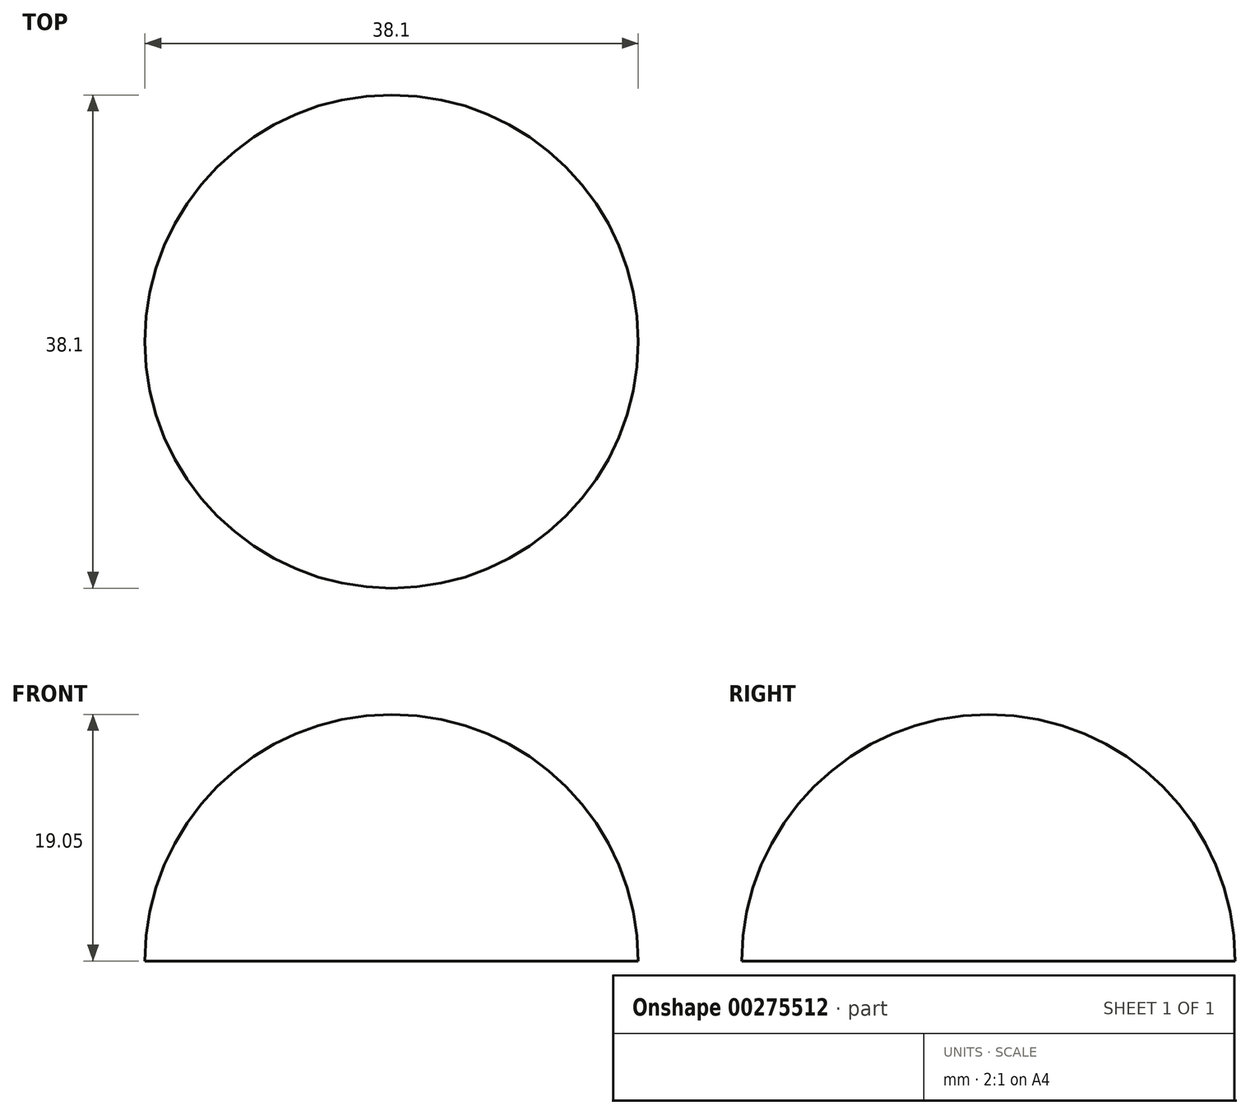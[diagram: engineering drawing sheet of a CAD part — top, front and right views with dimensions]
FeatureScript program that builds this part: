
annotation { "Feature Type Name" : "Feature", "Feature Type Description" : "" }
export const myFeature = defineFeature(function(context is Context, id is Id, definition is map)
    precondition{}
    {
        {
            var Q0;
            Q0=qCreatedBy(makeId("Top.planeOp"),FACE);
            var sketch = newSketch(context, id + "F0", { "sketchPlane" : qUnion([Q0])});
            skArc(sketch, "E0", {"start": v(0, -19.05) * mm, "mid": v(19.05, 0) * mm, "end": v(0, 19.05) * mm});
            skLineSegment(sketch, "E1.left", {"start": v(0, 19.05) * mm, "end": v(0, -19.05) * mm});
            skPoint(sketch, "E2.orphan", {"position": v(0, 24.82) * mm});
            skSolve(sketch);
        }
        {
            var Q0;
            Q0=makeQuery(id+"F0.imprint","IMPRINT",FACE,{"disambiguationData":[TD([[makeQuery(id+"F0.imprint","IMPRINT",EDGE,{"derivedFrom":sQuery(id+"F0.wireOp",EDGE,"E0")}),1.0]])]});
            var Q1;
            Q1=sQuery(id+"F0.wireOp",EDGE,"E1.left");
            revolve(context, id + "F1", {"entities" : qUnion([Q0]), "axis" : qUnion([Q1]), "revolveType" : RevolveType.FULL});
        }
        {
            var Q0;
            Q0=qCreatedBy(makeId("Top.planeOp"),FACE);
            var sketch = newSketch(context, id + "F2", { "sketchPlane" : qUnion([Q0])});
            skLineSegment(sketch, "E3.bottom", {"start": v(0, 34.82) * mm, "end": v(29.36, 34.82) * mm});
            skLineSegment(sketch, "E3.top", {"start": v(0, -41.73) * mm, "end": v(29.36, -41.73) * mm});
            skLineSegment(sketch, "E3.left", {"start": v(0, 34.82) * mm, "end": v(0, -41.73) * mm});
            skLineSegment(sketch, "E3.right", {"start": v(29.36, 34.82) * mm, "end": v(29.36, -41.73) * mm});
            skSolve(sketch);
        }
        {
            var Q0;
            Q0=makeQuery(id+"F2.imprint","IMPRINT",FACE,{"disambiguationData":[TD([[makeQuery(id+"F2.imprint","IMPRINT",EDGE,{"derivedFrom":sQuery(id+"F2.wireOp",EDGE,"E3.bottom")}),-1.0]])]});
            extrude(context, id + "F3", {"entities" : qUnion([Q0]), "operationType" : NewBodyOperationType.REMOVE, "oppositeDirection" : true, "depth" : 50.8 * mm});
        }
        {
            var Q0;
            Q0=qCreatedBy(makeId("Right.planeOp"),FACE);
            var sketch = newSketch(context, id + "F4", { "sketchPlane" : qUnion([Q0])});
            skLineSegment(sketch, "E4.bottom", {"start": v(-34.54, 0) * mm, "end": v(41.73, 0) * mm});
            skLineSegment(sketch, "E4.top", {"start": v(-34.54, -38.57) * mm, "end": v(41.73, -38.57) * mm});
            skLineSegment(sketch, "E4.left", {"start": v(-34.54, 0) * mm, "end": v(-34.54, -38.57) * mm});
            skLineSegment(sketch, "E4.right", {"start": v(41.73, 0) * mm, "end": v(41.73, -38.57) * mm});
            skSolve(sketch);
        }
        {
            var Q0;
            Q0 = qSketchRegion(id + "F4", true);
            extrude(context, id + "F5", {"entities" : qUnion([Q0]), "operationType" : NewBodyOperationType.REMOVE, "oppositeDirection" : true, "depth" : 25.4 * mm});
        }
    });
